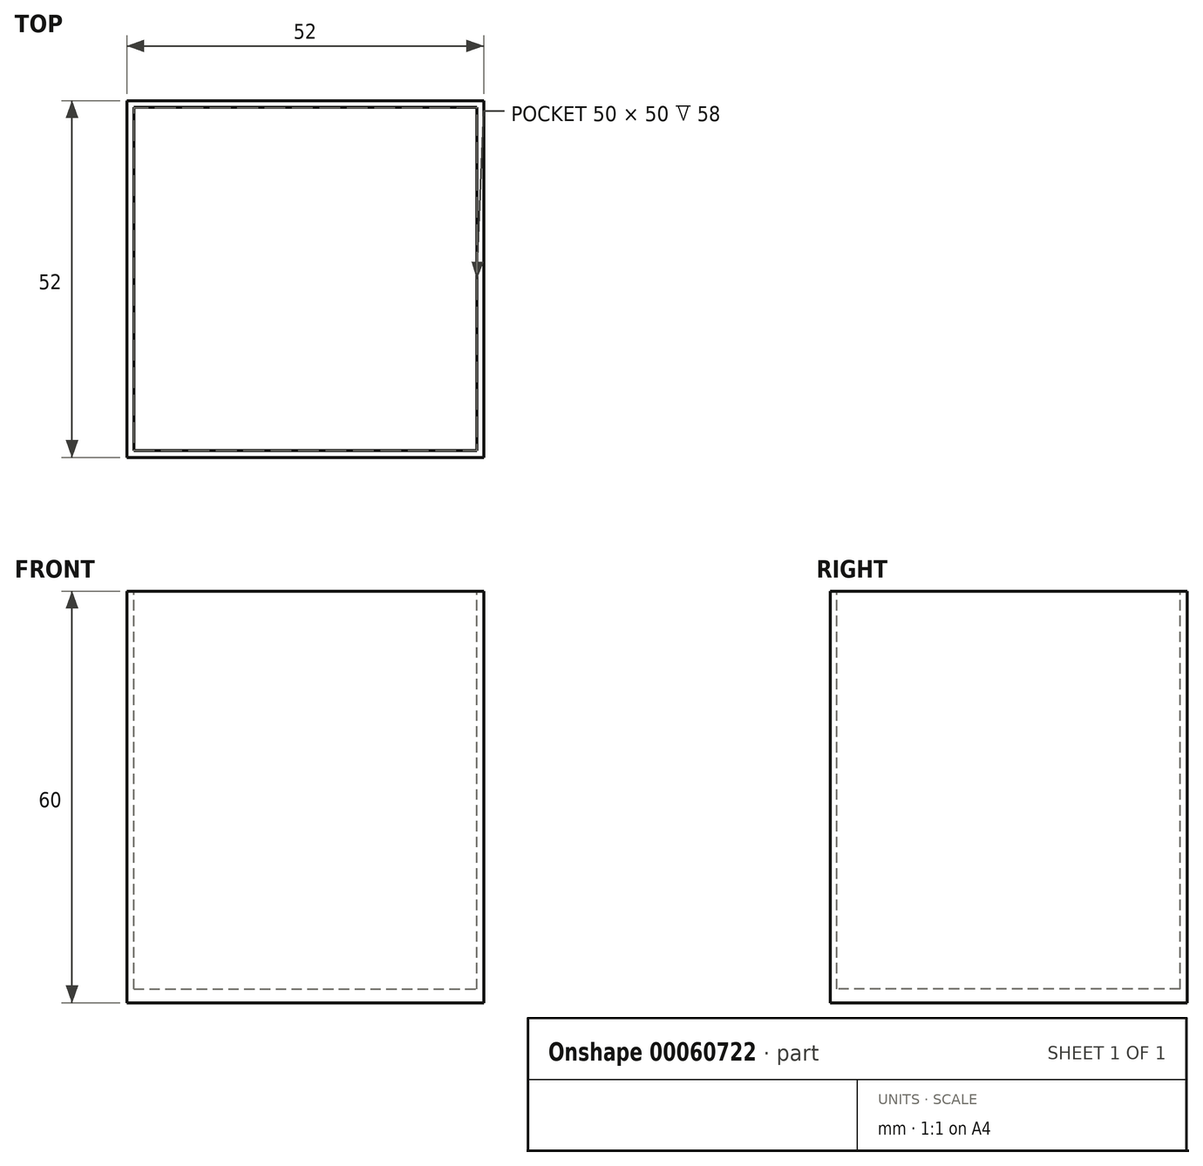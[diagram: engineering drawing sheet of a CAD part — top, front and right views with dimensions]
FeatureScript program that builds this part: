
annotation { "Feature Type Name" : "Feature", "Feature Type Description" : "" }
export const myFeature = defineFeature(function(context is Context, id is Id, definition is map)
    precondition{}
    {
        {
            var Q0;
            Q0=qCreatedBy(makeId("Top.planeOp"),FACE);
            var sketch = newSketch(context, id + "F0", { "sketchPlane" : qUnion([Q0])});
            skLineSegment(sketch, "E0.bottom", {"start": v(-49.61, 0.93) * mm, "end": v(2.39, 0.93) * mm});
            skLineSegment(sketch, "E0.top", {"start": v(-49.61, -51.07) * mm, "end": v(2.39, -51.07) * mm});
            skLineSegment(sketch, "E0.left", {"start": v(-49.61, 0.93) * mm, "end": v(-49.61, -51.07) * mm});
            skLineSegment(sketch, "E0.right", {"start": v(2.39, 0.93) * mm, "end": v(2.39, -51.07) * mm});
            skSolve(sketch);
        }
        {
            var Q0;
            Q0=makeQuery(id+"F0.imprint","IMPRINT",FACE,{"disambiguationData":[TD([[makeQuery(id+"F0.imprint","IMPRINT",EDGE,{"derivedFrom":sQuery(id+"F0.wireOp",EDGE,"E0.bottom")}),-1.0]])]});
            extrude(context, id + "F1", {"entities" : qUnion([Q0]), "depth" : 60 * mm});
        }
        {
            var Q0;
            Q0=makeQuery(id+"F1.opExtrude","CAP_FACE",FACE,{"disambiguationData":[OSD([sQuery(id+"F0.wireOp",EDGE,"E0.bottom"),sQuery(id+"F0.wireOp",EDGE,"E0.top"),sQuery(id+"F0.wireOp",EDGE,"E0.left"),sQuery(id+"F0.wireOp",EDGE,"E0.right")])],"isStart":false});
            var sketch = newSketch(context, id + "F2", { "sketchPlane" : qUnion([Q0])});
            skLineSegment(sketch, "E1.bottom", {"start": v(-48.61, -0.07) * mm, "end": v(1.39, -0.07) * mm});
            skLineSegment(sketch, "E1.top", {"start": v(-48.61, -50.07) * mm, "end": v(1.39, -50.07) * mm});
            skLineSegment(sketch, "E1.left", {"start": v(-48.61, -0.07) * mm, "end": v(-48.61, -50.07) * mm});
            skLineSegment(sketch, "E1.right", {"start": v(1.39, -0.07) * mm, "end": v(1.39, -50.07) * mm});
            skLineSegment(sketch, "E2", {"start": v(-23.61, 0.93) * mm, "end": v(-23.61, -51.07) * mm, "construction": true});
            skLineSegment(sketch, "E3", {"start": v(-49.61, -25.07) * mm, "end": v(2.39, -25.07) * mm, "construction": true});
            skSolve(sketch);
        }
        {
            var Q0;
            Q0 = qSketchRegion(id + "F2", true);
            extrude(context, id + "F3", {"entities" : qUnion([Q0]), "operationType" : NewBodyOperationType.REMOVE, "oppositeDirection" : true, "depth" : 58 * mm});
        }
    });
